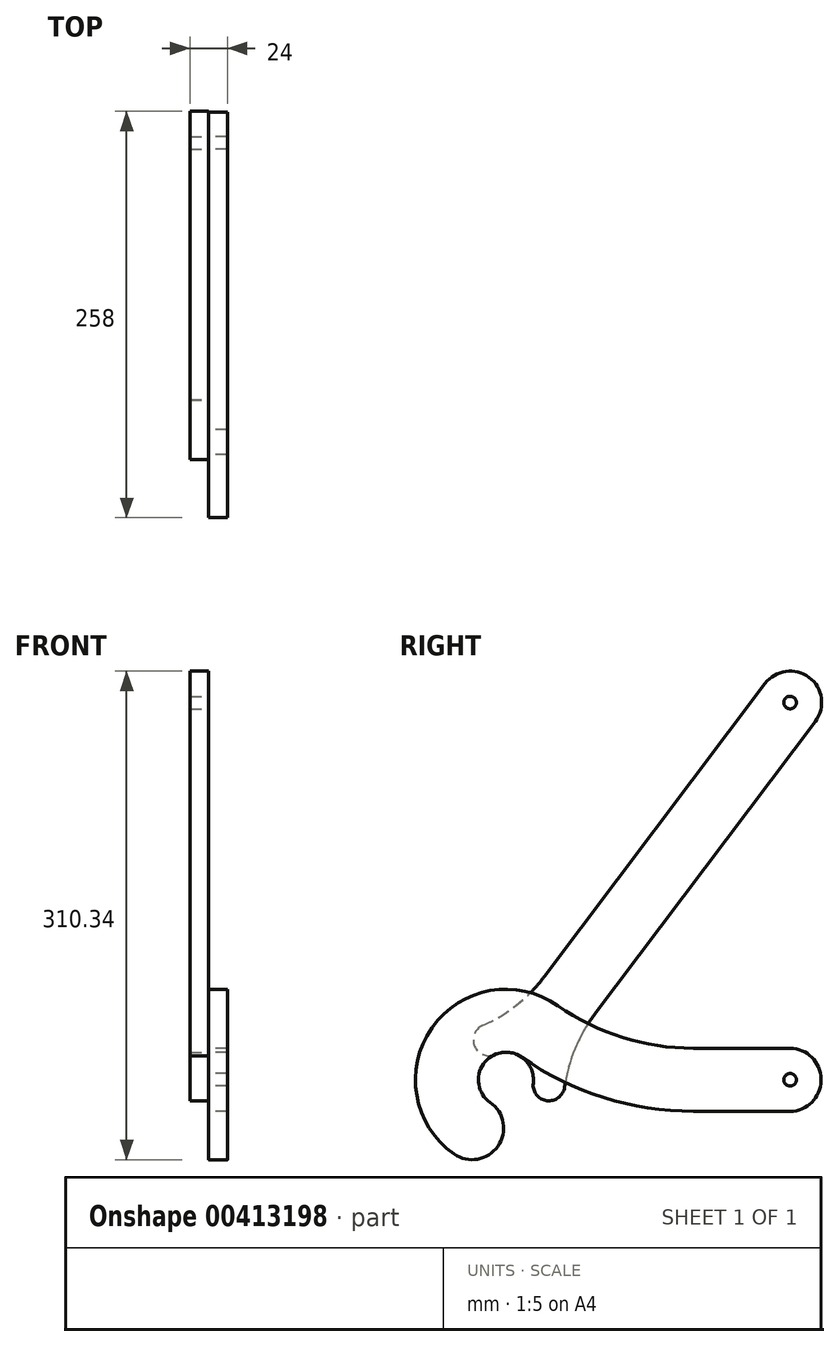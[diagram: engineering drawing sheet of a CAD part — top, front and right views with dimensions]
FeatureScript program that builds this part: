
annotation { "Feature Type Name" : "Feature", "Feature Type Description" : "" }
export const myFeature = defineFeature(function(context is Context, id is Id, definition is map)
    precondition{}
    {
        {
            var Q0;
            Q0=qCreatedBy(makeId("Right.planeOp"),FACE);
            var sketch = newSketch(context, id + "F0", { "sketchPlane" : qUnion([Q0])});
            skArc(sketch, "E0", {"start": v(-189.96, 14.34) * mm, "mid": v(-214.34, 10.04) * mm, "end": v(-210.04, -14.34) * mm});
            skArc(sketch, "E1", {"start": v(-167.02, 47.1) * mm, "mid": v(-247.1, 32.98) * mm, "end": v(-232.98, -47.1) * mm});
            skLineSegment(sketch, "E2.bottom", {"start": v(-81.07, 20) * mm, "end": v(-19.5, 20) * mm});
            skLineSegment(sketch, "E2.top", {"start": v(-81.07, -20) * mm, "end": v(-19.5, -20) * mm});
            skLineSegment(sketch, "E2.right", {"start": v(0, 0.5) * mm, "end": v(0, -0.5) * mm});
            skPoint(sketch, "E3.visualSharp", {"position": v(0, 20) * mm});
            skArc(sketch, "E3.filletArc", {"start": v(0, 0.5) * mm, "mid": v(-5.71, 14.29) * mm, "end": v(-19.5, 20) * mm});
            skPoint(sketch, "E4.visualSharp", {"position": v(0, -20) * mm});
            skArc(sketch, "E4.filletArc", {"start": v(-19.5, -20) * mm, "mid": v(-5.71, -14.29) * mm, "end": v(0, -0.5) * mm});
            skCircle(sketch, "E5", {"center": v(-19.5, 0) * mm, "radius": 4 * mm});
            skPoint(sketch, "E6.visualSharp", {"position": v(-146.1, 20) * mm});
            skArc(sketch, "E6.filletArc", {"start": v(-167.02, 47.1) * mm, "mid": v(-126.13, 26.94) * mm, "end": v(-81.07, 20) * mm});
            skArc(sketch, "E7", {"start": v(-232.98, -47.1) * mm, "mid": v(-205.13, -42.19) * mm, "end": v(-210.04, -14.34) * mm});
            skLineSegment(sketch, "E8", {"start": v(-200, 0) * mm, "end": v(-221.5, -30.72) * mm, "construction": true});
            skLineSegment(sketch, "E9", {"start": v(-200, 0) * mm, "end": v(-200, -66.7) * mm, "construction": true});
            skArc(sketch, "E10", {"start": v(-189.96, 14.34) * mm, "mid": v(-138.16, -11.21) * mm, "end": v(-81.07, -20) * mm});
            skLineSegment(sketch, "E11", {"start": v(-189.96, 14.34) * mm, "end": v(-110.4, -41.38) * mm, "construction": true});
            skSolve(sketch);
        }
        {
            var Q0;
            Q0=makeQuery(id+"F0.imprint","IMPRINT",FACE,{"disambiguationData":[TD([[makeQuery(id+"F0.imprint","IMPRINT",EDGE,{"derivedFrom":sQuery(id+"F0.wireOp",EDGE,"E0")}),-1.0]])]});
            extrude(context, id + "F1", {"entities" : qUnion([Q0]), "depth" : 12 * mm});
        }
        {
            var Q0;
            Q0=qCreatedBy(makeId("Right.planeOp"),FACE);
            var sketch = newSketch(context, id + "F2", { "sketchPlane" : qUnion([Q0])});
            skLineSegment(sketch, "E12", {"start": v(-19.5, 0) * mm, "end": v(-19.5, 233.26) * mm, "construction": true});
            skCircle(sketch, "E13", {"center": v(-19.5, 239.62) * mm, "radius": 4 * mm});
            skArc(sketch, "E14", {"start": v(-182.63, -2.13) * mm, "mid": v(-189.47, 13.98) * mm, "end": v(-206.84, 16.1) * mm});
            skArc(sketch, "E15", {"start": v(-214.81, 34.45) * mm, "mid": v(-219.92, 21.32) * mm, "end": v(-206.84, 16.1) * mm});
            skArc(sketch, "E16", {"start": v(-182.63, -2.13) * mm, "mid": v(-174, -13.26) * mm, "end": v(-162.8, -4.73) * mm});
            skLineSegment(sketch, "E17", {"start": v(-35.47, 251.66) * mm, "end": v(-175.59, 65.65) * mm});
            skArc(sketch, "E18", {"start": v(-214.81, 34.45) * mm, "mid": v(-193.22, 47.55) * mm, "end": v(-175.59, 65.65) * mm});
            skArc(sketch, "E19", {"start": v(-143.64, 41.58) * mm, "mid": v(-156.17, 19.64) * mm, "end": v(-162.8, -4.73) * mm});
            skLineSegment(sketch, "E20", {"start": v(-19.5, 239.62) * mm, "end": v(-200, 0) * mm, "construction": true});
            skLineSegment(sketch, "E21.trimOffspring", {"start": v(-143.64, 41.58) * mm, "end": v(-3.53, 227.6) * mm});
            skArc(sketch, "E22.trimOffspring", {"start": v(-3.53, 227.6) * mm, "mid": v(-7.47, 255.6) * mm, "end": v(-35.47, 251.66) * mm});
            skLineSegment(sketch, "E23", {"start": v(-210.75, 25.31) * mm, "end": v(-200, 0) * mm, "construction": true});
            skLineSegment(sketch, "E24", {"start": v(-200, 0) * mm, "end": v(-172.7, -3.35) * mm, "construction": true});
            skSolve(sketch);
        }
        {
            var Q0;
            Q0 = qSketchRegion(id + "F2", true);
            extrude(context, id + "F3", {"entities" : qUnion([Q0]), "oppositeDirection" : true, "depth" : 12 * mm});
        }
    });
